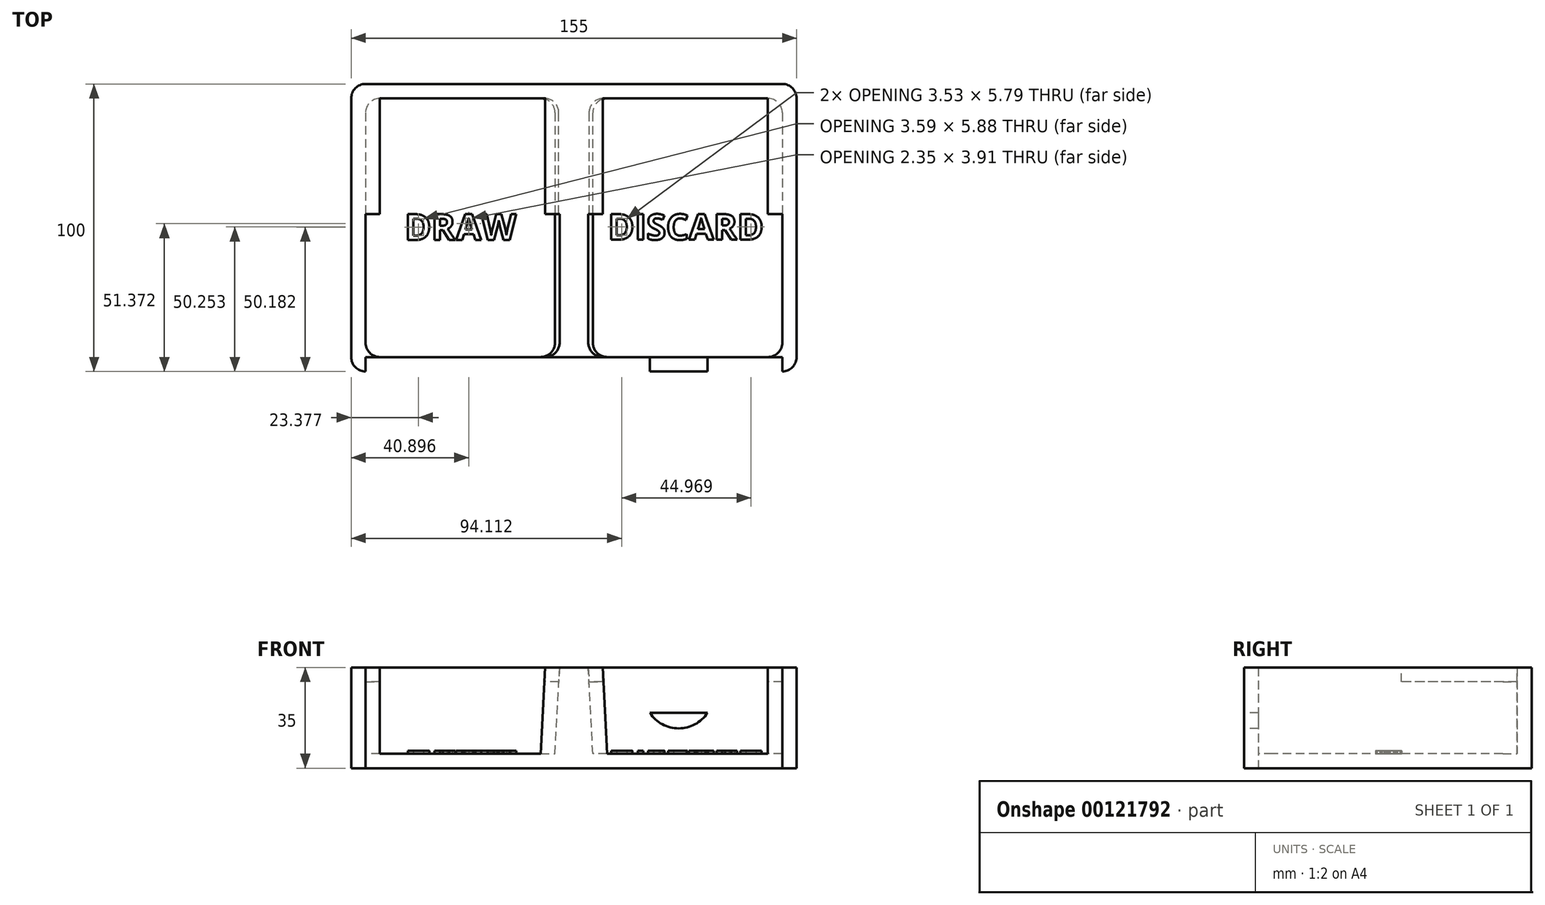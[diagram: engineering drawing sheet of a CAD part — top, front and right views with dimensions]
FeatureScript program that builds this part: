
annotation { "Feature Type Name" : "Feature", "Feature Type Description" : "" }
export const myFeature = defineFeature(function(context is Context, id is Id, definition is map)
    precondition{}
    {
        {
            var Q0;
            Q0=qCreatedBy(makeId("Top.planeOp"),FACE);
            var sketch = newSketch(context, id + "F0", { "sketchPlane" : qUnion([Q0])});
            skLineSegment(sketch, "E0.bottom", {"start": v(-76.97, 45.23) * mm, "end": v(78.03, 45.23) * mm});
            skLineSegment(sketch, "E0.top", {"start": v(-76.97, -54.77) * mm, "end": v(78.03, -54.77) * mm});
            skLineSegment(sketch, "E0.left", {"start": v(-76.97, 45.23) * mm, "end": v(-76.97, -54.77) * mm});
            skLineSegment(sketch, "E0.right", {"start": v(78.03, 45.23) * mm, "end": v(78.03, -54.77) * mm});
            skLineSegment(sketch, "E1", {"start": v(-6.97, 45.23) * mm, "end": v(-6.97, -54.77) * mm});
            skLineSegment(sketch, "E2", {"start": v(8.03, 45.23) * mm, "end": v(8.03, -54.77) * mm});
            skSolve(sketch);
        }
        {
            var Q0;
            Q0=makeQuery(id+"F0.imprint","IMPRINT",FACE,{"disambiguationData":[TD([[makeQuery(id+"F0.imprint","IMPRINT",EDGE,{"derivedFrom":sQuery(id+"F0.wireOp",EDGE,"E0.bottom")}),-1.0]])]});
            extrude(context, id + "F1", {"entities" : qUnion([Q0]), "depth" : 35 * mm});
        }
        {
            var Q0;
            Q0=makeQuery(id+"F1.opExtrude","SWEPT_EDGE",EDGE,{"disambiguationData":[OSD([sQuery(id+"F0.wireOp",EDGE,"E0.bottom"),sQuery(id+"F0.wireOp",EDGE,"E0.left")])]});
            var Q1;
            Q1=makeQuery(id+"F1.opExtrude","SWEPT_EDGE",EDGE,{"disambiguationData":[OSD([sQuery(id+"F0.wireOp",EDGE,"E0.bottom"),sQuery(id+"F0.wireOp",EDGE,"E0.right")])]});
            var Q2;
            Q2=makeQuery(id+"F1.opExtrude","SWEPT_EDGE",EDGE,{"disambiguationData":[OSD([sQuery(id+"F0.wireOp",EDGE,"E0.top"),sQuery(id+"F0.wireOp",EDGE,"E0.left")])]});
            var Q3;
            Q3=makeQuery(id+"F1.opExtrude","SWEPT_EDGE",EDGE,{"disambiguationData":[OSD([sQuery(id+"F0.wireOp",EDGE,"E0.top"),sQuery(id+"F0.wireOp",EDGE,"E0.right")])]});
            fillet(context, id + "F2", {"entities" : qUnion([Q0, Q1, Q2, Q3]), "radius" : 5 * mm, "tangentPropagation" : true, "allowEdgeOverflow" : false});
        }
        {
            var Q0;
            Q0=makeQuery(id+"F1.opExtrude","CAP_FACE",FACE,{"disambiguationData":[OSD([sQuery(id+"F0.wireOp",EDGE,"E0.bottom"),sQuery(id+"F0.wireOp",EDGE,"E0.top"),sQuery(id+"F0.wireOp",EDGE,"E0.left"),sQuery(id+"F0.wireOp",EDGE,"E0.right")])],"isStart":false});
            shell(context, id + "F3", {"entities" : qUnion([Q0]), "thickness" : 5 * mm});
        }
        {
            var Q0;
            Q0=makeQuery(id+"F1.opExtrude","CAP_FACE",FACE,{"disambiguationData":[OSD([sQuery(id+"F0.wireOp",EDGE,"E0.bottom"),sQuery(id+"F0.wireOp",EDGE,"E0.top"),sQuery(id+"F0.wireOp",EDGE,"E0.left"),sQuery(id+"F0.wireOp",EDGE,"E0.right")])],"isStart":false});
            var sketch = newSketch(context, id + "F4", { "sketchPlane" : qUnion([Q0])});
            skLineSegment(sketch, "E3.bottom", {"start": v(-4.47, 40.23) * mm, "end": v(5.53, 40.23) * mm});
            skLineSegment(sketch, "E3.top", {"start": v(-4.47, -49.77) * mm, "end": v(5.53, -49.77) * mm});
            skLineSegment(sketch, "E3.left", {"start": v(-4.47, 40.23) * mm, "end": v(-4.47, -49.77) * mm});
            skLineSegment(sketch, "E3.right", {"start": v(5.53, 40.23) * mm, "end": v(5.53, -49.77) * mm});
            skLineSegment(sketch, "E4.bottom", {"start": v(-71.97, 40.23) * mm, "end": v(-66.97, 40.23) * mm});
            skLineSegment(sketch, "E4.top", {"start": v(-71.97, 0) * mm, "end": v(-66.97, 0) * mm});
            skLineSegment(sketch, "E4.left", {"start": v(-71.97, 40.23) * mm, "end": v(-71.97, 0) * mm});
            skLineSegment(sketch, "E4.right", {"start": v(-66.97, 40.23) * mm, "end": v(-66.97, 0) * mm});
            skLineSegment(sketch, "E5.bottom", {"start": v(-4.47, 40.23) * mm, "end": v(-9.47, 40.23) * mm});
            skLineSegment(sketch, "E5.top", {"start": v(-4.47, 0) * mm, "end": v(-9.47, 0) * mm});
            skLineSegment(sketch, "E5.left", {"start": v(-4.47, 40.23) * mm, "end": v(-4.47, 0) * mm});
            skLineSegment(sketch, "E5.right", {"start": v(-9.47, 40.23) * mm, "end": v(-9.47, 0) * mm});
            skLineSegment(sketch, "E6.bottom", {"start": v(5.53, 40.23) * mm, "end": v(10.53, 40.23) * mm});
            skLineSegment(sketch, "E6.top", {"start": v(5.53, 0) * mm, "end": v(10.53, 0) * mm});
            skLineSegment(sketch, "E6.left", {"start": v(5.53, 40.23) * mm, "end": v(5.53, 0) * mm});
            skLineSegment(sketch, "E6.right", {"start": v(10.53, 40.23) * mm, "end": v(10.53, 0) * mm});
            skLineSegment(sketch, "E7.bottom", {"start": v(73.03, 40.23) * mm, "end": v(68.03, 40.23) * mm});
            skLineSegment(sketch, "E7.top", {"start": v(73.03, 0) * mm, "end": v(68.03, 0) * mm});
            skLineSegment(sketch, "E7.left", {"start": v(73.03, 40.23) * mm, "end": v(73.03, 0) * mm});
            skLineSegment(sketch, "E7.right", {"start": v(68.03, 40.23) * mm, "end": v(68.03, 0) * mm});
            skSolve(sketch);
        }
        {
            var Q0;
            Q0=makeQuery(id+"F4.imprint","IMPRINT",FACE,{"disambiguationData":[TD([[makeQuery(id+"F4.imprint","IMPRINT",EDGE,{"derivedFrom":sQuery(id+"F4.wireOp",EDGE,"E3.bottom")}),-1.0]])]});
            extrude(context, id + "F5", {"entities" : qUnion([Q0]), "operationType" : NewBodyOperationType.ADD, "oppositeDirection" : true, "depth" : 35 * mm, "hasDraft" : true, "draftAngle" : 3 * degree});
        }
        {
            var Q0;
            Q0=makeQuery(id+"F4.imprint","IMPRINT",FACE,{"disambiguationData":[TD([[makeQuery(id+"F4.imprint","IMPRINT",EDGE,{"derivedFrom":sQuery(id+"F4.wireOp",EDGE,"E4.bottom")}),-1.0]])]});
            var Q1;
            Q1=makeQuery(id+"F4.imprint","IMPRINT",FACE,{"disambiguationData":[TD([[makeQuery(id+"F4.imprint","IMPRINT",EDGE,{"derivedFrom":sQuery(id+"F4.wireOp",EDGE,"E5.bottom")}),-1.0]])]});
            var Q2;
            Q2=makeQuery(id+"F4.imprint","IMPRINT",FACE,{"disambiguationData":[TD([[makeQuery(id+"F4.imprint","IMPRINT",EDGE,{"derivedFrom":sQuery(id+"F4.wireOp",EDGE,"E6.bottom")}),-1.0]])]});
            var Q3;
            Q3=makeQuery(id+"F4.imprint","IMPRINT",FACE,{"disambiguationData":[TD([[makeQuery(id+"F4.imprint","IMPRINT",EDGE,{"derivedFrom":sQuery(id+"F4.wireOp",EDGE,"E7.bottom")}),-1.0]])]});
            extrude(context, id + "F6", {"entities" : qUnion([Q0, Q1, Q2, Q3]), "operationType" : NewBodyOperationType.ADD, "oppositeDirection" : true, "depth" : 5 * mm});
        }
        {
            var Q0;
            Q0=makeQuery(id+"F3.opShell","OFFSET_EDGE",EDGE,{"disambiguationData":[OSD([sQuery(id+"F0.wireOp",EDGE,"E0.top"),sQuery(id+"F0.wireOp",EDGE,"E0.right")])]});
            var Q1;
            Q1=makeQuery(id+"F5.boolean.opBoolean","INTERSECT",EDGE,{"derivedFrom":[makeQuery(id+"F3.opShell","OFFSET_FACE",FACE,{"disambiguationData":[OSD([sQuery(id+"F0.wireOp",EDGE,"E0.top")])]}),makeQuery(id+"F5.opExtrude","SWEPT_FACE",FACE,{"disambiguationData":[OSD([sQuery(id+"F4.wireOp",EDGE,"E3.left"),sQuery(id+"F4.wireOp",EDGE,"E5.left")])]})]});
            var Q2;
            Q2=makeQuery(id+"F3.opShell","OFFSET_EDGE",EDGE,{"disambiguationData":[OSD([sQuery(id+"F0.wireOp",EDGE,"E0.top"),sQuery(id+"F0.wireOp",EDGE,"E0.left")])]});
            var Q3;
            Q3=makeQuery(id+"F5.boolean.opBoolean","INTERSECT",EDGE,{"derivedFrom":[makeQuery(id+"F3.opShell","OFFSET_FACE",FACE,{"disambiguationData":[OSD([sQuery(id+"F0.wireOp",EDGE,"E0.top")])]}),makeQuery(id+"F5.opExtrude","SWEPT_FACE",FACE,{"disambiguationData":[OSD([sQuery(id+"F4.wireOp",EDGE,"E3.right"),sQuery(id+"F4.wireOp",EDGE,"E6.left")])]})]});
            var Q4;
            Q4=makeQuery(id+"F5.boolean.opBoolean","INTERSECT",EDGE,{"derivedFrom":[makeQuery(id+"F3.opShell","OFFSET_FACE",FACE,{"disambiguationData":[OSD([sQuery(id+"F0.wireOp",EDGE,"E0.bottom")])]}),makeQuery(id+"F5.opExtrude","SWEPT_FACE",FACE,{"disambiguationData":[OSD([sQuery(id+"F4.wireOp",EDGE,"E3.right"),sQuery(id+"F4.wireOp",EDGE,"E6.left")])]})]});
            var Q5;
            Q5=makeQuery(id+"F3.opShell","OFFSET_EDGE",EDGE,{"disambiguationData":[OSD([sQuery(id+"F0.wireOp",EDGE,"E0.bottom"),sQuery(id+"F0.wireOp",EDGE,"E0.right")])]});
            var Q6;
            Q6=makeQuery(id+"F5.boolean.opBoolean","INTERSECT",EDGE,{"derivedFrom":[makeQuery(id+"F3.opShell","OFFSET_FACE",FACE,{"disambiguationData":[OSD([sQuery(id+"F0.wireOp",EDGE,"E0.bottom")])]}),makeQuery(id+"F5.opExtrude","SWEPT_FACE",FACE,{"disambiguationData":[OSD([sQuery(id+"F4.wireOp",EDGE,"E3.left"),sQuery(id+"F4.wireOp",EDGE,"E5.left")])]})]});
            var Q7;
            Q7=makeQuery(id+"F3.opShell","OFFSET_EDGE",EDGE,{"disambiguationData":[OSD([sQuery(id+"F0.wireOp",EDGE,"E0.bottom"),sQuery(id+"F0.wireOp",EDGE,"E0.left")])]});
            fillet(context, id + "F7", {"entities" : qUnion([Q0, Q1, Q2, Q3, Q4, Q5, Q6, Q7]), "radius" : 5 * mm, "tangentPropagation" : true, "allowEdgeOverflow" : false});
        }
        {
            var Q0;
            Q0=makeQuery(id+"F1.opExtrude","SWEPT_FACE",FACE,{"disambiguationData":[OSD([sQuery(id+"F0.wireOp",EDGE,"E0.top")])]});
            var sketch = newSketch(context, id + "F8", { "sketchPlane" : qUnion([Q0])});
            skLineSegment(sketch, "E8.bottom", {"start": v(-11.97, 35) * mm, "end": v(-61.97, 35) * mm});
            skLineSegment(sketch, "E8.top", {"start": v(-11.97, 19.2) * mm, "end": v(-61.97, 19.2) * mm});
            skLineSegment(sketch, "E8.left", {"start": v(-11.97, 35) * mm, "end": v(-11.97, 19.2) * mm});
            skLineSegment(sketch, "E8.right", {"start": v(-61.97, 35) * mm, "end": v(-61.97, 19.2) * mm});
            skArc(sketch, "E9", {"start": v(-46.97, 19.2) * mm, "mid": v(-36.97, 13.84) * mm, "end": v(-26.97, 19.2) * mm});
            skArc(sketch, "E10.MirrorCS", {"start": v(46.97, 19.2) * mm, "mid": v(36.97, 13.84) * mm, "end": v(26.97, 19.2) * mm});
            skLineSegment(sketch, "E11.MirrorCS", {"start": v(11.97, 19.2) * mm, "end": v(61.97, 19.2) * mm});
            skLineSegment(sketch, "E12.MirrorCS", {"start": v(61.97, 35) * mm, "end": v(61.97, 19.2) * mm});
            skLineSegment(sketch, "E13.MirrorCS", {"start": v(11.97, 35) * mm, "end": v(11.97, 19.2) * mm});
            skLineSegment(sketch, "E14.MirrorCS", {"start": v(11.97, 35) * mm, "end": v(61.97, 35) * mm});
            skSolve(sketch);
        }
        {
            var Q0;
            Q0=makeQuery(id+"F8.imprint","IMPRINT",FACE,{"disambiguationData":[TD([[makeQuery(id+"F8.imprint","IMPRINT",EDGE,{"derivedFrom":sQuery(id+"F8.wireOp",EDGE,"E8.bottom")}),-1.0]])]});
            var Q1;
            {var subQ0=sQuery(id+"F8.wireOp",EDGE,"E9");Q1=makeQuery(id+"F8.imprint","IMPRINT",FACE,{"disambiguationData":[TD([[makeQuery(id+"F8.imprint","IMPRINT",EDGE,{"derivedFrom":subQ0}),1.0]])]});}
            var Q2;
            {var subQ0=sQuery(id+"F8.wireOp",EDGE,"E12.MirrorCS");Q2=makeQuery(id+"F8.imprint","IMPRINT",FACE,{"disambiguationData":[TD([[makeQuery(id+"F8.imprint","IMPRINT",EDGE,{"derivedFrom":subQ0}),-1.0]])]});}
            var Q3;
            {var subQ0=sQuery(id+"F8.wireOp",EDGE,"E10.MirrorCS");Q3=makeQuery(id+"F8.imprint","IMPRINT",FACE,{"disambiguationData":[TD([[makeQuery(id+"F8.imprint","IMPRINT",EDGE,{"derivedFrom":subQ0}),-1.0]])]});}
            var Q4;
            {var subQ2=sQuery(id+"F0.wireOp",EDGE,"E0.left");var subQ4=sQuery(id+"F0.wireOp",EDGE,"E0.top");Q4=makeQuery(id+"F5.boolean.opBoolean","SPLIT",FACE,{"disambiguationData":[TD([makeQuery(id+"F3.opShell","OFFSET_FACE",FACE,{"disambiguationData":[OSD([subQ2])]})])],"derivedFrom":makeQuery(id+"F3.opShell","OFFSET_FACE",FACE,{"disambiguationData":[OSD([subQ4])]})});}
            extrude(context, id + "F9", {"entities" : qUnion([Q0, Q1, Q2, Q3]), "operationType" : NewBodyOperationType.REMOVE, "endBound" : BoundingType.UP_TO_SURFACE, "oppositeDirection" : true, "endBoundEntityFace" : qUnion([Q4]), "depth" : 25 * mm});
        }
        {
            var Q0;
            {var subQ0=sQuery(id+"F0.wireOp",EDGE,"E0.bottom");var subQ1=sQuery(id+"F0.wireOp",EDGE,"E0.top");var subQ2=sQuery(id+"F0.wireOp",EDGE,"E0.left");Q0=makeQuery(id+"F5.boolean.opBoolean","SPLIT",FACE,{"disambiguationData":[TD([makeQuery(id+"F3.opShell","OFFSET_FACE",FACE,{"disambiguationData":[OSD([subQ2])]})])],"derivedFrom":makeQuery(id+"F3.opShell","OFFSET_FACE",FACE,{"disambiguationData":[OSD([subQ0,subQ1,subQ2,sQuery(id+"F0.wireOp",EDGE,"E0.right")])]})});}
            var sketch = newSketch(context, id + "F10", { "sketchPlane" : qUnion([Q0])});
            skText(sketch, "E15", { "text": "DRAW", "fontName": "OpenSans-Bold.ttf"});
            skText(sketch, "E16", { "text": "DISCARD", "fontName": "OpenSans-Bold.ttf"});
            const initialGuessF10  = {"E15": [-0.05844, -0.00911, 1, 0, 0.00911], "E16": [0.01237, -0.00897, 1, 0, 0.00897]};
            skSetInitialGuess(sketch, initialGuessF10);
            skSolve(sketch);
        }
        {
            var Q0;
            Q0 = qSketchRegion(id + "F10", true);
            extrude(context, id + "F11", {"entities" : qUnion([Q0]), "depth" : 1 * mm});
        }
    });
